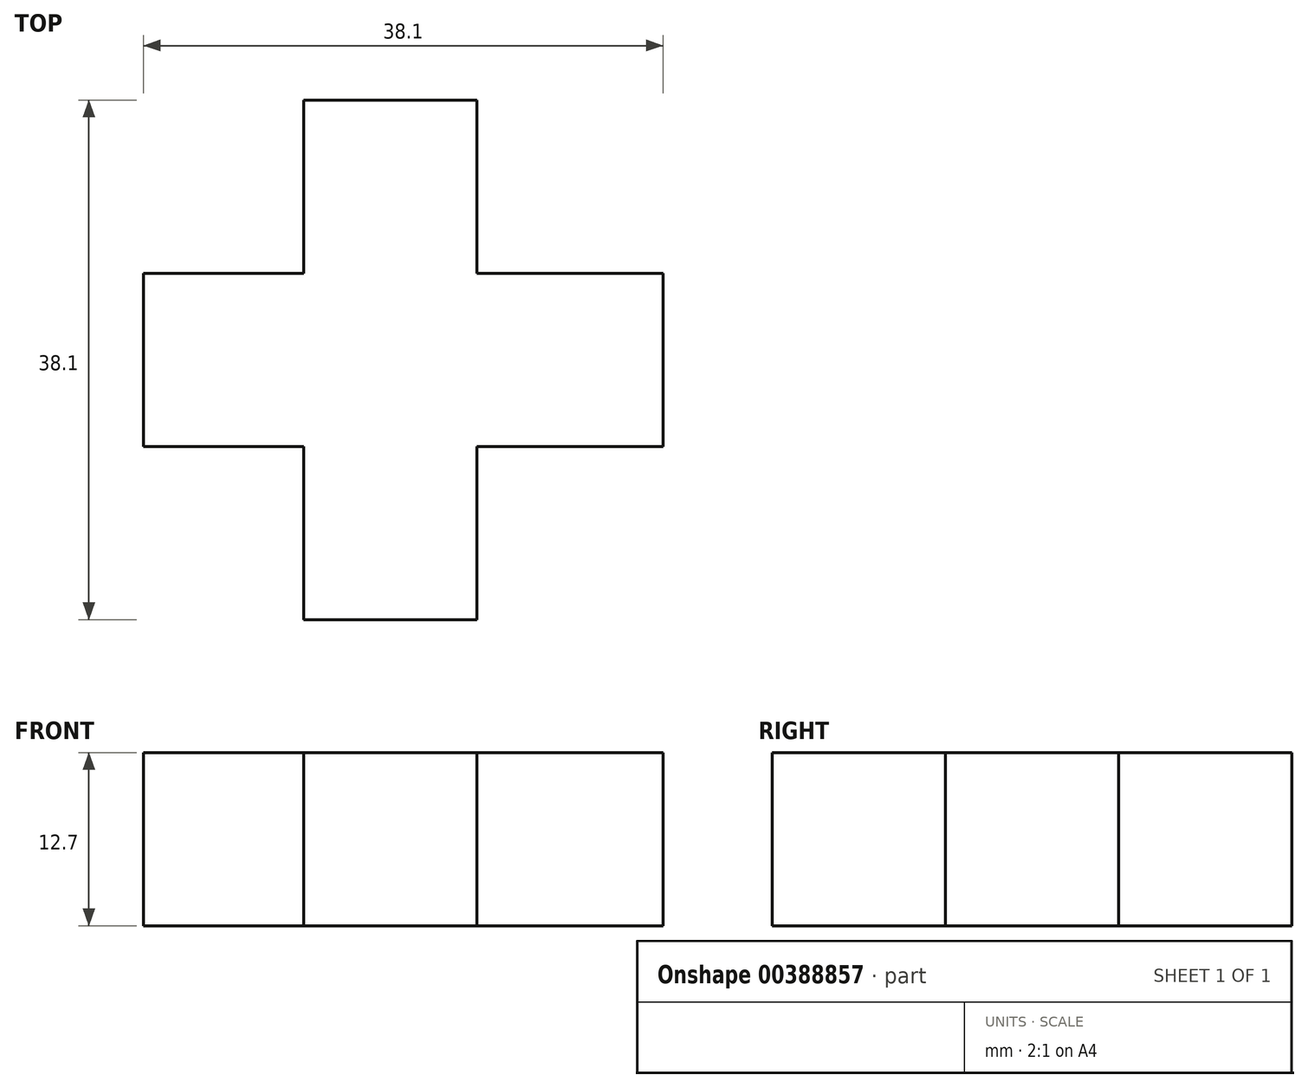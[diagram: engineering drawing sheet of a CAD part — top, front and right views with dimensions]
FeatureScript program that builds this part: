
annotation { "Feature Type Name" : "Feature", "Feature Type Description" : "" }
export const myFeature = defineFeature(function(context is Context, id is Id, definition is map)
    precondition{}
    {
        {
            var Q0;
            Q0=qCreatedBy(makeId("Top.planeOp"),FACE);
            var sketch = newSketch(context, id + "F0", { "sketchPlane" : qUnion([Q0])});
            skLineSegment(sketch, "E0.bottom", {"start": v(0, 0) * mm, "end": v(12.7, 0) * mm});
            skLineSegment(sketch, "E0.top", {"start": v(0, 38.1) * mm, "end": v(12.7, 38.1) * mm});
            skLineSegment(sketch, "E0.left", {"start": v(0, 0) * mm, "end": v(0, 12.7) * mm});
            skLineSegment(sketch, "E0.right", {"start": v(12.7, 0) * mm, "end": v(12.7, 12.7) * mm});
            skLineSegment(sketch, "E1.bottom", {"start": v(-11.76, 25.4) * mm, "end": v(0, 25.4) * mm});
            skLineSegment(sketch, "E1.top", {"start": v(-11.76, 12.7) * mm, "end": v(0, 12.7) * mm});
            skLineSegment(sketch, "E1.left", {"start": v(-11.76, 25.4) * mm, "end": v(-11.76, 12.7) * mm});
            skLineSegment(sketch, "E1.right", {"start": v(26.34, 25.4) * mm, "end": v(26.34, 12.7) * mm});
            skLineSegment(sketch, "E2.top", {"start": v(0, 25.4) * mm, "end": v(-11.76, 25.4) * mm});
            skLineSegment(sketch, "E2.left", {"start": v(0, 38.1) * mm, "end": v(0, 25.4) * mm});
            skLineSegment(sketch, "E3.trimOffspring", {"start": v(12.7, 25.4) * mm, "end": v(12.7, 38.1) * mm});
            skLineSegment(sketch, "E4.trimOffspring", {"start": v(0, 25.4) * mm, "end": v(0, 38.1) * mm});
            skLineSegment(sketch, "E5.trimOffspring", {"start": v(12.7, 12.7) * mm, "end": v(26.34, 12.7) * mm});
            skLineSegment(sketch, "E6.trimOffspring", {"start": v(12.7, 25.4) * mm, "end": v(26.34, 25.4) * mm});
            skSolve(sketch);
        }
        {
            var Q0;
            Q0=makeQuery(id+"F0.imprint","IMPRINT",FACE,{"disambiguationData":[TD([[makeQuery(id+"F0.imprint","IMPRINT",EDGE,{"derivedFrom":sQuery(id+"F0.wireOp",EDGE,"E0.bottom")}),1.0]])]});
            extrude(context, id + "F1", {"entities" : qUnion([Q0]), "depth" : 12.7 * mm});
        }
    });
